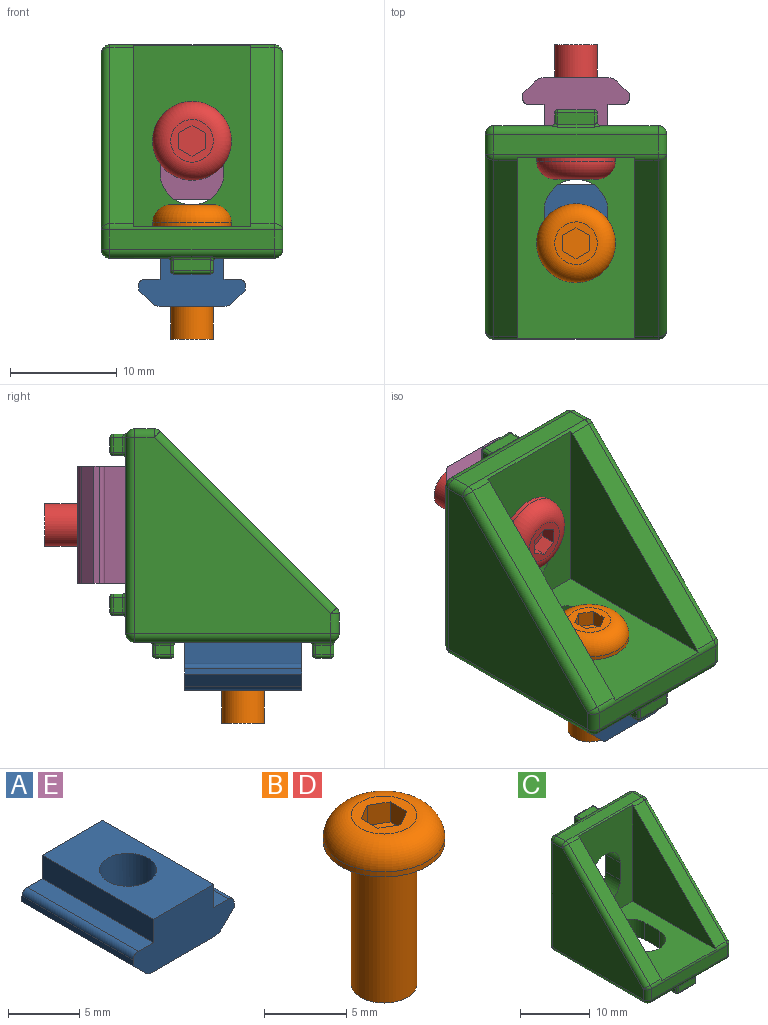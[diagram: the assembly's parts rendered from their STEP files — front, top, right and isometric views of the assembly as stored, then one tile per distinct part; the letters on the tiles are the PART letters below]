
ASSEMBLY  parts=5 mates=4
PART A: 17 faces, bbox 10x11x4.5 mm
  f0: plane 11x1.21mm, normal (-0.71,0,-0.71), area 18.8mm2, adj f1,f13,f14,f15
  f1: cylinder r=1mm len=11mm, axis (0,1,0), area 8.6mm2, adj f0,f2,f14,f15
  f2: plane 11x6.17mm, normal (0,0,-1), area 55.3mm2, adj f1,f3,f14,f15,f16
  f3: cylinder r=1mm len=11mm, axis (0,1,0), area 8.6mm2, adj f2,f4,f14,f15
  f4: plane 11x1.21mm, normal (0.71,0,-0.71), area 18.8mm2, adj f3,f5,f14,f15
  f5: plane 11x0.5mm, normal (1,0,0), area 5.5mm2, adj f4,f6,f14,f15
  f6: cylinder r=0.5mm len=11mm, axis (0,1,0), area 8.6mm2, adj f5,f7,f14,f15
  f7: plane 11x1.5mm, normal (0,0,1), area 16.5mm2, adj f6,f8,f14,f15
  f8: plane 11x2mm, normal (1,0,0), area 22mm2, adj f7,f9,f14,f15
  f9: plane 11x6mm, normal (0,0,1), area 53.4mm2, adj f8,f10,f14,f15,f16
  f10: plane 11x2mm, normal (-1,0,0), area 22mm2, adj f9,f11,f14,f15
  f11: plane 11x1.5mm, normal (0,0,1), area 16.5mm2, adj f10,f12,f14,f15
  f12: cylinder r=0.5mm len=11mm, axis (0,1,0), area 8.6mm2, adj f11,f13,f14,f15
  f13: plane 11x0.5mm, normal (-1,0,0), area 5.5mm2, adj f0,f12,f14,f15
  f14: plane 10x4.5mm, normal (0,-1,0), area 34.6mm2, adj f0,f1,f2,f3,f4,f5,f6,f7
  f15: plane 10x4.5mm, normal (0,1,0), area 34.6mm2, adj f0,f1,f2,f3,f4,f5,f6,f7
  f16: cylinder r=2mm len=4.5mm, axis (0,0,1), area 56.5mm2, adj f2,f9
PART B: 14 faces, bbox 8x8x12.6 mm
  f0: plane 4x4mm, normal (0,0,1), area 7.2mm2, adj f5,f6,f7,f8,f9,f10,f11
  f1: cylinder r=2mm len=10.4mm, axis (0,0,1), area 130.7mm2, adj f2,f13
  f2: torus R=2.2mm, axis (0,0,1), area 4.1mm2, adj f1,f3
  f3: plane 7.4x7.4mm, normal (0,0,-1), area 27.8mm2, adj f2,f4
  f4: cylinder r=3.7mm len=7.4mm, axis (0,0,1), area 8.8mm2, adj f3,f5
  f5: torus R=2mm, axis (0,0,1), area 49.9mm2, adj f0,f4
  f6: plane 1.5x1.25mm, normal (-0.5,-0.87,0), area 2.2mm2, adj f0,f7,f11,f12
  f7: plane 1.5x1.25mm, normal (0.5,-0.87,0), area 2.2mm2, adj f0,f6,f8,f12
  f8: plane 1.5x1.44mm, normal (1,0,0), area 2.2mm2, adj f0,f7,f9,f12
  f9: plane 1.5x1.25mm, normal (0.5,0.87,0), area 2.2mm2, adj f0,f8,f10,f12
  f10: plane 1.5x1.25mm, normal (-0.5,0.87,0), area 2.2mm2, adj f0,f9,f11,f12
  f11: plane 1.5x1.44mm, normal (-1,0,0), area 2.2mm2, adj f0,f6,f10,f12
  f12: plane 2.89x2.5mm, normal (0,0,1), area 5.4mm2, adj f6,f7,f8,f9,f10,f11
  f13: plane 4x4mm, normal (0,0,-1), area 12.6mm2, adj f1
PART C: 145 faces, bbox 17x21.5x21.5 mm
  f0: cylinder r=0.8mm len=15.4mm, axis (1,0,0), area 17.4mm2, adj f3,f7,f46,f47,f139,f142,f144
  f1: plane 18.4x15.4mm, normal (0,1,0), area 216.4mm2, adj f2,f13,f14,f15,f17,f44,f49,f53
  f2: cylinder r=0.8mm len=15.4mm, axis (1,0,0), area 17.4mm2, adj f1,f16,f54,f57,f79,f82,f84
  f3: plane 18.4x15.4mm, normal (0,0,-1), area 216.4mm2, adj f0,f8,f9,f10,f11,f42,f43,f44
  f4: plane 16.93x11mm, normal (0,0,1), area 139.9mm2, adj f5,f8,f9,f10,f11,f19,f21,f51
  f5: plane 16.93x11mm, normal (0,-1,0), area 139.9mm2, adj f4,f13,f14,f15,f17,f19,f21,f64
  f6: plane 18.4x18.4mm, normal (-1,0,0), area 201.9mm2, adj f43,f52,f53,f60,f61
  f7: plane 15.4x1.87mm, normal (0,-1,0), area 28.8mm2, adj f0,f50,f51,f52
  f8: plane 3x3mm, normal (1,0,0), area 9mm2, adj f3,f4,f9,f11
  f9: cylinder r=3mm len=6mm, axis (0,0,-1), area 28.3mm2, adj f3,f4,f8,f10
  f10: plane 3x3mm, normal (-1,0,0), area 9mm2, adj f3,f4,f9,f11
  f11: cylinder r=3mm len=6mm, axis (0,0,-1), area 28.3mm2, adj f3,f4,f8,f10
  f12: plane 18.4x18.4mm, normal (1,0,0), area 201.9mm2, adj f42,f49,f50,f58,f59
  f13: plane 3x3mm, normal (-1,0,0), area 9mm2, adj f1,f5,f14,f17
  f14: cylinder r=3mm len=6mm, axis (0,1,0), area 28.3mm2, adj f1,f5,f13,f15
  f15: plane 3x3mm, normal (1,0,0), area 9mm2, adj f1,f5,f14,f17
  f16: plane 15.4x1.87mm, normal (0,0,1), area 28.8mm2, adj f2,f58,f61,f64
  f17: cylinder r=3mm len=6mm, axis (0,1,0), area 28.3mm2, adj f1,f5,f13,f15
  f18: plane 16.53x16.53mm, normal (0,-0.71,0.71), area 51.4mm2, adj f19,f51,f59,f64
  f19: plane 16.93x16.93mm, normal (-1,0,0), area 144.5mm2, adj f4,f5,f18,f51,f64
  f20: plane 16.53x16.53mm, normal (0,-0.71,0.71), area 51.4mm2, adj f21,f51,f60,f64
  f21: plane 16.93x16.93mm, normal (1,0,0), area 144.5mm2, adj f4,f5,f20,f51,f64
  f22: plane 3.4x0.9mm, normal (0,1,0), area 3.1mm2, adj f108,f109,f118,f119
  f23: plane 1.4x0.9mm, normal (-1,0,0), area 1.3mm2, adj f105,f108,f112,f113
  f24: plane 3.4x0.9mm, normal (0,-1,0), area 3.1mm2, adj f111,f112,f120,f121
  f25: plane 1.4x0.9mm, normal (1,0,0), area 1.3mm2, adj f110,f119,f120,f124
  f26: plane 3.4x1.4mm, normal (0,0,-1), area 4.8mm2, adj f105,f109,f110,f111
  f27: plane 3.4x0.9mm, normal (0,1,0), area 3.1mm2, adj f127,f128,f136,f137
  f28: plane 1.4x0.9mm, normal (-1,0,0), area 1.3mm2, adj f126,f127,f130,f135
  f29: plane 3.4x1.08mm, normal (0,-1,0), area 3.7mm2, adj f134,f135,f141,f142
  f30: plane 1.4x0.9mm, normal (1,0,0), area 1.3mm2, adj f133,f137,f141,f143
  f31: plane 3.4x1.4mm, normal (0,0,-1), area 4.8mm2, adj f126,f128,f133,f134
  f32: plane 3.4x0.9mm, normal (0,0,-1), area 3.1mm2, adj f67,f68,f76,f77
  f33: plane 1.4x0.9mm, normal (-1,0,0), area 1.3mm2, adj f73,f77,f81,f83
  f34: plane 3.4x1.08mm, normal (0,0,1), area 3.7mm2, adj f74,f75,f81,f82
  f35: plane 1.4x0.9mm, normal (1,0,0), area 1.3mm2, adj f66,f67,f70,f75
  f36: plane 3.4x1.4mm, normal (0,1,0), area 4.8mm2, adj f66,f68,f73,f74
  f37: plane 3.4x0.9mm, normal (0,0,1), area 3.1mm2, adj f88,f89,f98,f99
  f38: plane 1.4x0.9mm, normal (1,0,0), area 1.3mm2, adj f85,f89,f90,f91
  f39: plane 3.4x0.9mm, normal (0,0,-1), area 3.1mm2, adj f91,f92,f100,f101
  f40: plane 1.4x0.9mm, normal (-1,0,0), area 1.3mm2, adj f93,f98,f101,f104
  f41: plane 3.4x1.4mm, normal (0,1,0), area 4.8mm2, adj f85,f88,f92,f93
  f42: cylinder r=0.8mm len=18.4mm, axis (0,1,0), area 23.1mm2, adj f3,f12,f45,f46
  f43: cylinder r=0.8mm len=18.4mm, axis (0,-1,0), area 23.1mm2, adj f3,f6,f47,f48
  f44: cylinder r=0.8mm len=15.4mm, axis (-1,0,0), area 19.4mm2, adj f1,f3,f45,f48
  f45: sphere r=0.8mm, area 1mm2, adj f42,f44,f49
  f46: sphere r=0.8mm, area 1mm2, adj f0,f42,f50
  f47: sphere r=0.8mm, area 1mm2, adj f0,f43,f52
  f48: sphere r=0.8mm, area 1mm2, adj f43,f44,f53
  f49: cylinder r=0.8mm len=18.4mm, axis (0,0,-1), area 23.1mm2, adj f1,f12,f45,f54
  f50: cylinder r=0.8mm len=1.87mm, axis (0,0,1), area 2.3mm2, adj f7,f12,f46,f55
  f51: cylinder r=0.8mm len=15.4mm, axis (-1,0,0), area 6.5mm2, adj f4,f7,f18,f19,f20,f21,f55,f56
  f52: cylinder r=0.8mm len=1.87mm, axis (0,0,-1), area 2.3mm2, adj f6,f7,f47,f56
  f53: cylinder r=0.8mm len=18.4mm, axis (0,0,1), area 23.1mm2, adj f1,f6,f48,f57
  f54: sphere r=0.8mm, area 1mm2, adj f2,f49,f58
  f55: sphere r=0.8mm, area 0.5mm2, adj f50,f51,f59
  f56: sphere r=0.8mm, area 0.5mm2, adj f51,f52,f60
  f57: sphere r=0.8mm, area 1mm2, adj f2,f53,f61
  f58: cylinder r=0.8mm len=1.87mm, axis (0,-1,0), area 2.3mm2, adj f12,f16,f54,f62
  f59: cylinder r=0.8mm len=17.1mm, axis (0,0.71,0.71), area 29.4mm2, adj f12,f18,f55,f62
  f60: cylinder r=0.8mm len=17.1mm, axis (0,0.71,0.71), area 29.4mm2, adj f6,f20,f56,f63
  f61: cylinder r=0.8mm len=1.87mm, axis (0,1,0), area 2.3mm2, adj f6,f16,f57,f63
  f62: sphere r=0.8mm, area 0.5mm2, adj f58,f59,f64
  f63: sphere r=0.8mm, area 0.5mm2, adj f60,f61,f64
  f64: cylinder r=0.8mm len=15.4mm, axis (-1,0,0), area 6.5mm2, adj f5,f16,f18,f19,f20,f21,f62,f63
  f65: sphere r=0.3mm, area 0.1mm2, adj f66,f67,f68
  f66: cylinder r=0.3mm len=1.4mm, axis (0,0,1), area 0.7mm2, adj f35,f36,f65,f69
  f67: cylinder r=0.3mm len=0.9mm, axis (0,-1,0), area 0.4mm2, adj f32,f35,f65,f71
  f68: cylinder r=0.3mm len=3.4mm, axis (1,0,0), area 1.6mm2, adj f32,f36,f65,f72
  f69: sphere r=0.3mm, area 0.1mm2, adj f66,f74,f75
  f70: cylinder r=0.3mm len=1.4mm, axis (0,0,-1), area 0.7mm2, adj f1,f35,f71,f79
  f71: torus R=0.6mm, axis (0,1,0), area 0.3mm2, adj f1,f67,f70,f76
  f72: sphere r=0.3mm, area 0.1mm2, adj f68,f73,f77
  f73: cylinder r=0.3mm len=1.4mm, axis (0,0,-1), area 0.7mm2, adj f33,f36,f72,f78
  f74: cylinder r=0.3mm len=3.4mm, axis (-1,0,0), area 1.6mm2, adj f34,f36,f69,f78
  f75: cylinder r=0.3mm len=1.08mm, axis (0,1,0), area 0.5mm2, adj f34,f35,f69,f79
  f76: cylinder r=0.3mm len=3.4mm, axis (-1,0,0), area 1.6mm2, adj f1,f32,f71,f80
  f77: cylinder r=0.3mm len=0.9mm, axis (0,1,0), area 0.4mm2, adj f32,f33,f72,f80
  f78: sphere r=0.3mm, area 0.1mm2, adj f73,f74,f81
  f79: bspline ~0.66x0.52mm, area 0.2mm2, adj f2,f70,f75,f82
  f80: torus R=0.6mm, axis (0,1,0), area 0.3mm2, adj f1,f76,f77,f83
  f81: cylinder r=0.3mm len=1.08mm, axis (0,-1,0), area 0.5mm2, adj f33,f34,f78,f84
  f82: cylinder r=0.3mm len=3.4mm, axis (1,0,0), area 1mm2, adj f2,f34,f79,f84
  f83: cylinder r=0.3mm len=1.4mm, axis (0,0,1), area 0.7mm2, adj f1,f33,f80,f84
  f84: bspline ~0.72x0.48mm, area 0.2mm2, adj f2,f81,f82,f83
  f85: cylinder r=0.3mm len=1.4mm, axis (0,0,1), area 0.7mm2, adj f38,f41,f86,f87
  f86: sphere r=0.3mm, area 0.1mm2, adj f85,f88,f89
  f87: sphere r=0.3mm, area 0.1mm2, adj f85,f91,f92
  f88: cylinder r=0.3mm len=3.4mm, axis (-1,0,0), area 1.6mm2, adj f37,f41,f86,f94
  f89: cylinder r=0.3mm len=0.9mm, axis (0,1,0), area 0.4mm2, adj f37,f38,f86,f95
  f90: cylinder r=0.3mm len=1.4mm, axis (0,0,-1), area 0.7mm2, adj f1,f38,f95,f96
  f91: cylinder r=0.3mm len=0.9mm, axis (0,-1,0), area 0.4mm2, adj f38,f39,f87,f96
  f92: cylinder r=0.3mm len=3.4mm, axis (1,0,0), area 1.6mm2, adj f39,f41,f87,f97
  f93: cylinder r=0.3mm len=1.4mm, axis (0,0,-1), area 0.7mm2, adj f40,f41,f94,f97
  f94: sphere r=0.3mm, area 0.1mm2, adj f88,f93,f98
  f95: torus R=0.6mm, axis (0,1,0), area 0.3mm2, adj f1,f89,f90,f99
  f96: torus R=0.6mm, axis (0,1,0), area 0.3mm2, adj f1,f90,f91,f100
  f97: sphere r=0.3mm, area 0.1mm2, adj f92,f93,f101
  f98: cylinder r=0.3mm len=0.9mm, axis (0,-1,0), area 0.4mm2, adj f37,f40,f94,f102
  f99: cylinder r=0.3mm len=3.4mm, axis (1,0,0), area 1.6mm2, adj f1,f37,f95,f102
  f100: cylinder r=0.3mm len=3.4mm, axis (-1,0,0), area 1.6mm2, adj f1,f39,f96,f103
  f101: cylinder r=0.3mm len=0.9mm, axis (0,1,0), area 0.4mm2, adj f39,f40,f97,f103
  f102: torus R=0.6mm, axis (0,1,0), area 0.3mm2, adj f1,f98,f99,f104
  f103: torus R=0.6mm, axis (0,1,0), area 0.3mm2, adj f1,f100,f101,f104
  f104: cylinder r=0.3mm len=1.4mm, axis (0,0,1), area 0.7mm2, adj f1,f40,f102,f103
  f105: cylinder r=0.3mm len=1.4mm, axis (0,1,0), area 0.7mm2, adj f23,f26,f106,f107
  f106: sphere r=0.3mm, area 0.1mm2, adj f105,f108,f109
  f107: sphere r=0.3mm, area 0.1mm2, adj f105,f111,f112
  f108: cylinder r=0.3mm len=0.9mm, axis (0,0,-1), area 0.4mm2, adj f22,f23,f106,f114
  f109: cylinder r=0.3mm len=3.4mm, axis (1,0,0), area 1.6mm2, adj f22,f26,f106,f115
  f110: cylinder r=0.3mm len=1.4mm, axis (0,-1,0), area 0.7mm2, adj f25,f26,f115,f116
  f111: cylinder r=0.3mm len=3.4mm, axis (-1,0,0), area 1.6mm2, adj f24,f26,f107,f116
  f112: cylinder r=0.3mm len=0.9mm, axis (0,0,1), area 0.4mm2, adj f23,f24,f107,f117
  f113: cylinder r=0.3mm len=1.4mm, axis (0,-1,0), area 0.7mm2, adj f3,f23,f114,f117
  f114: torus R=0.6mm, axis (0,0,1), area 0.3mm2, adj f3,f108,f113,f118
  f115: sphere r=0.3mm, area 0.1mm2, adj f109,f110,f119
  f116: sphere r=0.3mm, area 0.1mm2, adj f110,f111,f120
  f117: torus R=0.6mm, axis (0,0,1), area 0.3mm2, adj f3,f112,f113,f121
  f118: cylinder r=0.3mm len=3.4mm, axis (-1,0,0), area 1.6mm2, adj f3,f22,f114,f122
  f119: cylinder r=0.3mm len=0.9mm, axis (0,0,1), area 0.4mm2, adj f22,f25,f115,f122
  f120: cylinder r=0.3mm len=0.9mm, axis (0,0,-1), area 0.4mm2, adj f24,f25,f116,f123
  f121: cylinder r=0.3mm len=3.4mm, axis (1,0,0), area 1.6mm2, adj f3,f24,f117,f123
  f122: torus R=0.6mm, axis (0,0,1), area 0.3mm2, adj f3,f118,f119,f124
  f123: torus R=0.6mm, axis (0,0,1), area 0.3mm2, adj f3,f120,f121,f124
  f124: cylinder r=0.3mm len=1.4mm, axis (0,1,0), area 0.7mm2, adj f3,f25,f122,f123
  f125: sphere r=0.3mm, area 0.1mm2, adj f126,f127,f128
  f126: cylinder r=0.3mm len=1.4mm, axis (0,1,0), area 0.7mm2, adj f28,f31,f125,f129
  f127: cylinder r=0.3mm len=0.9mm, axis (0,0,-1), area 0.4mm2, adj f27,f28,f125,f131
  f128: cylinder r=0.3mm len=3.4mm, axis (1,0,0), area 1.6mm2, adj f27,f31,f125,f132
  f129: sphere r=0.3mm, area 0.1mm2, adj f126,f134,f135
  f130: cylinder r=0.3mm len=1.4mm, axis (0,-1,0), area 0.7mm2, adj f3,f28,f131,f139
  f131: torus R=0.6mm, axis (0,0,1), area 0.3mm2, adj f3,f127,f130,f136
  f132: sphere r=0.3mm, area 0.1mm2, adj f128,f133,f137
  f133: cylinder r=0.3mm len=1.4mm, axis (0,-1,0), area 0.7mm2, adj f30,f31,f132,f138
  f134: cylinder r=0.3mm len=3.4mm, axis (-1,0,0), area 1.6mm2, adj f29,f31,f129,f138
  f135: cylinder r=0.3mm len=1.08mm, axis (0,0,1), area 0.5mm2, adj f28,f29,f129,f139
  f136: cylinder r=0.3mm len=3.4mm, axis (-1,0,0), area 1.6mm2, adj f3,f27,f131,f140
  f137: cylinder r=0.3mm len=0.9mm, axis (0,0,1), area 0.4mm2, adj f27,f30,f132,f140
  f138: sphere r=0.3mm, area 0.1mm2, adj f133,f134,f141
  f139: bspline ~0.66x0.52mm, area 0.2mm2, adj f0,f130,f135,f142
  f140: torus R=0.6mm, axis (0,0,1), area 0.3mm2, adj f3,f136,f137,f143
  f141: cylinder r=0.3mm len=1.08mm, axis (0,0,-1), area 0.5mm2, adj f29,f30,f138,f144
  f142: cylinder r=0.3mm len=3.4mm, axis (1,0,0), area 1mm2, adj f0,f29,f139,f144
  f143: cylinder r=0.3mm len=1.4mm, axis (0,1,0), area 0.7mm2, adj f3,f30,f140,f144
  f144: bspline ~0.72x0.48mm, area 0.2mm2, adj f0,f141,f142,f143
PART D: same geometry as B
PART E: same geometry as A
PLACE A t=(0,-50,-5)mm
PLACE B at identity
PLACE C t=(0,-29,-5)mm
PLACE D rot(axis=(1,0,0),90deg) t=(0,-24,36)mm
PLACE E rot(axis=(1,0,0),90deg) t=(0,-19,-14)mm
MATE fastened C.f14 <-> D.f2  axis (0,-1,0) through (0,-22,6)mm
MATE fastened C.f11 <-> B.f2  axis (0,0,1) through (0,-30,-2)mm
MATE fastened E.f16 <-> C.f14  axis (0,-1,0) through (0,-19,6)mm
MATE fastened A.f16 <-> C.f11  axis (0,0,1) through (0,-30,-5)mm
